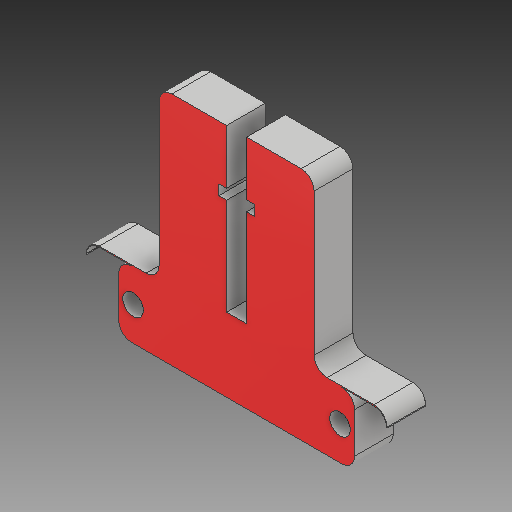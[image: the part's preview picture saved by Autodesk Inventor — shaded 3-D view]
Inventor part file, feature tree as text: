
AUTODESK INVENTOR PART (.ipt)
format: ipt  version: 2018 (Build 220112000, 112)  size: 378,880 bytes
history: native  units: in
note: dims shown in document units (in); Inventor stores cm internally (conversion verified against a paired STEP export)
features: extrude x5, sketch x5, projected_geometry x3, fillet x1
ambient origin geometry x8: Origin, YZ Plane, XZ Plane, XY Plane, X Axis, Y Axis, Z Axis, Center Point
bodies: Solid1 (feature_tree)
feature tree (14):
  extrude  "Extrusion1"  Depth=0.0787in
  extrude  "Extrusion2"  Depth=0.2362in TaperAngle=0.0deg
  fillet  "Fillet1"  Radius=0.0787in
  sketch  "Sketch3"  dims[d4=0.2362in d5=0.0in d6=0.2362in d7=0.0in d8=0.0787in]
  extrude  "Extrusion3"  Depth=0.0157in TaperAngle=0.0deg
  extrude  "Extrusion4"  [1 undecoded]
  extrude  "Extrusion5"  [1 undecoded]
  sketch  "Sketch1"  dims[d0=0.9449in d1=0.126in d2=0.126in d3=0.0787in]
  sketch  "Sketch4"  dims[d10=0.5118in d11=0.0in d12=0.0157in d13=0.0in]
  projected_geometry  "Projected Loop1"
  sketch  "Sketch5"  dims[d14=0.0039in d15=0.0in]
  projected_geometry  "Projected Loop2"
  projected_geometry  "Projected Loop3"
  sketch  "Sketch6"
note: 2 required parameter values undecoded (feature->parameter linkage not recoverable at this tier; creation-order binding heuristic only, values carry confidence <= 0.55)
